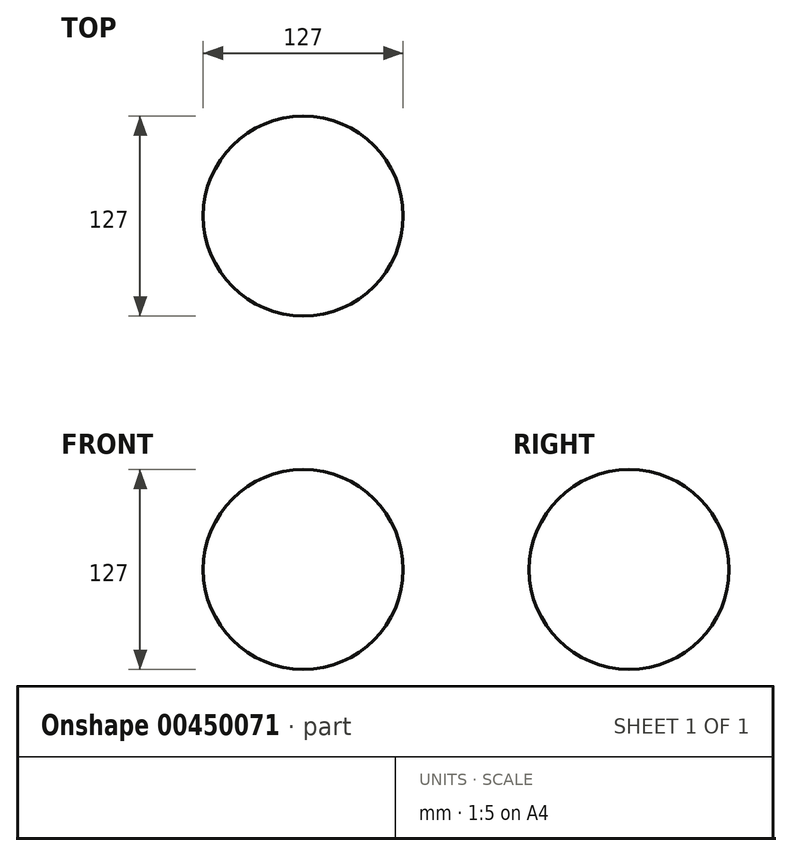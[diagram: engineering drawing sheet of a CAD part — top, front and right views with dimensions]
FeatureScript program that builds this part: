
annotation { "Feature Type Name" : "Feature", "Feature Type Description" : "" }
export const myFeature = defineFeature(function(context is Context, id is Id, definition is map)
    precondition{}
    {
        {
            var Q0;
            Q0=qCreatedBy(makeId("Top.planeOp"),FACE);
            var sketch = newSketch(context, id + "F0", { "sketchPlane" : qUnion([Q0])});
            skLineSegment(sketch, "E0", {"start": v(63.5, 0) * mm, "end": v(-63.5, 0) * mm});
            skLineSegment(sketch, "E1", {"start": v(-63.5, 0) * mm, "end": v(-63.5, 0) * mm});
            skArc(sketch, "E2", {"start": v(63.5, 0) * mm, "mid": v(0, 63.5) * mm, "end": v(-63.5, 0) * mm});
            skSolve(sketch);
        }
        {
            var Q0;
            Q0=makeQuery(id+"F0.imprint","IMPRINT",FACE,{"disambiguationData":[TD([[makeQuery(id+"F0.imprint","IMPRINT",EDGE,{"derivedFrom":sQuery(id+"F0.wireOp",EDGE,"E0")}),-1.0]])]});
            var Q1;
            Q1=sQuery(id+"F0.wireOp",EDGE,"E0");
            revolve(context, id + "F1", {"entities" : qUnion([Q0]), "axis" : qUnion([Q1]), "revolveType" : RevolveType.FULL});
        }
    });
